# Revit family: Wenger Cabinet 41
name_source: partatom
category: Furniture
revit_build: Autodesk Revit Architecture 2012 (Build: 20110916_2132(x64)
units: mm (PartAtom-declared; Revit-internal decimal feet)

## types (5) — shared parameters
Manufacturer = Wenger Corporation

## per-type parameters (varying)
| type | Cabinet Labeling | Description | Model | Plan Shelf Symbol | Shelving Style |
| Cabinet #41 - No Shelf | Labels : Standard | Cabinet #41 | 41 | Plan No Shelf | None |
| Cabinet #41 - Stationary | Labels : Standard-Line | Cabinet #41 - Stationary Shelf | 41S | Plan Line Shelf | Stationary |
| Cabinet #41 - Garment | Labels : Standard-circle | Cabinet #41 - Garment Storage | 41G | Plan Circle Shelf | Garment |
| Cabinet #41 - Revolving | Labels : Standard-circle | Cabinet #41 - Revolving Storage | 41R | Plan Circle Shelf | Revolving |
| Cabinet #41 - Flag | Labels : Standard-circle | Cabinet #41 - Flag Storage + Ring | 41FS | Plan Circle Shelf | Flag |

## geometry (parser evidence)
native form markers: Sweep x14
no freeform markers — native parametric forms only
